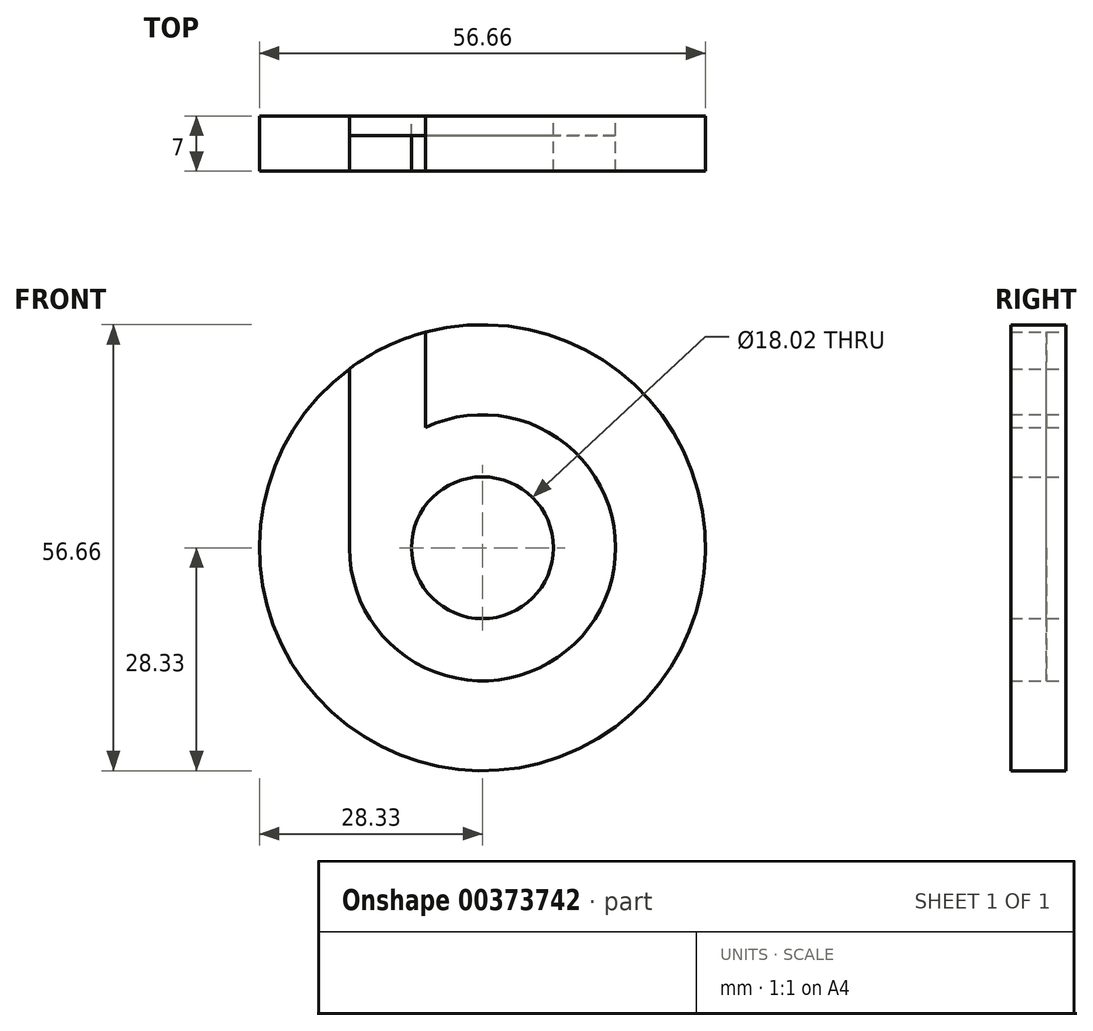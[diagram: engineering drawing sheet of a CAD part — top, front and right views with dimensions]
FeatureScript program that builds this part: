
annotation { "Feature Type Name" : "Feature", "Feature Type Description" : "" }
export const myFeature = defineFeature(function(context is Context, id is Id, definition is map)
    precondition{}
    {
        {
            var Q0;
            Q0=qCreatedBy(makeId("Front.planeOp"),FACE);
            var sketch = newSketch(context, id + "F0", { "sketchPlane" : qUnion([Q0])});
            skCircle(sketch, "E0", {"center": v(0, 0) * mm, "radius": 28.33 * mm});
            skArc(sketch, "E1", {"start": v(-16.9, 0) * mm, "mid": v(14.29, -9.04) * mm, "end": v(-7.24, 15.28) * mm});
            skLineSegment(sketch, "E2", {"start": v(-16.9, 0) * mm, "end": v(-16.9, 22.73) * mm});
            skCircle(sketch, "E3", {"center": v(0, 0) * mm, "radius": 9 * mm});
            skLineSegment(sketch, "E4", {"start": v(-7.24, 15.28) * mm, "end": v(-7.24, 27.38) * mm});
            skSolve(sketch);
        }
        {
            var Q0;
            Q0=makeQuery(id+"F0.imprint","IMPRINT",FACE,{"disambiguationData":[TD([[makeQuery(id+"F0.imprint","IMPRINT",EDGE,{"derivedFrom":sQuery(id+"F0.wireOp",EDGE,"E3")}),1.0]])]});
            extrude(context, id + "F1", {"entities" : qUnion([Q0]), "depth" : 7 * mm});
        }
        {
            var Q0;
            Q0=makeQuery(id+"F0.imprint","IMPRINT",FACE,{"disambiguationData":[TD([[makeQuery(id+"F0.imprint","IMPRINT",EDGE,{"derivedFrom":sQuery(id+"F0.wireOp",EDGE,"E1")}),-1.0]])]});
            extrude(context, id + "F2", {"entities" : qUnion([Q0]), "depth" : 7 * mm});
        }
        {
            var Q0;
            Q0=makeQuery(id+"F0.imprint","IMPRINT",FACE,{"disambiguationData":[TD([[makeQuery(id+"F0.imprint","IMPRINT",EDGE,{"derivedFrom":sQuery(id+"F0.wireOp",EDGE,"E1")}),1.0]])]});
            extrude(context, id + "F3", {"entities" : qUnion([Q0]), "depth" : 2.5 * mm});
        }
    });
